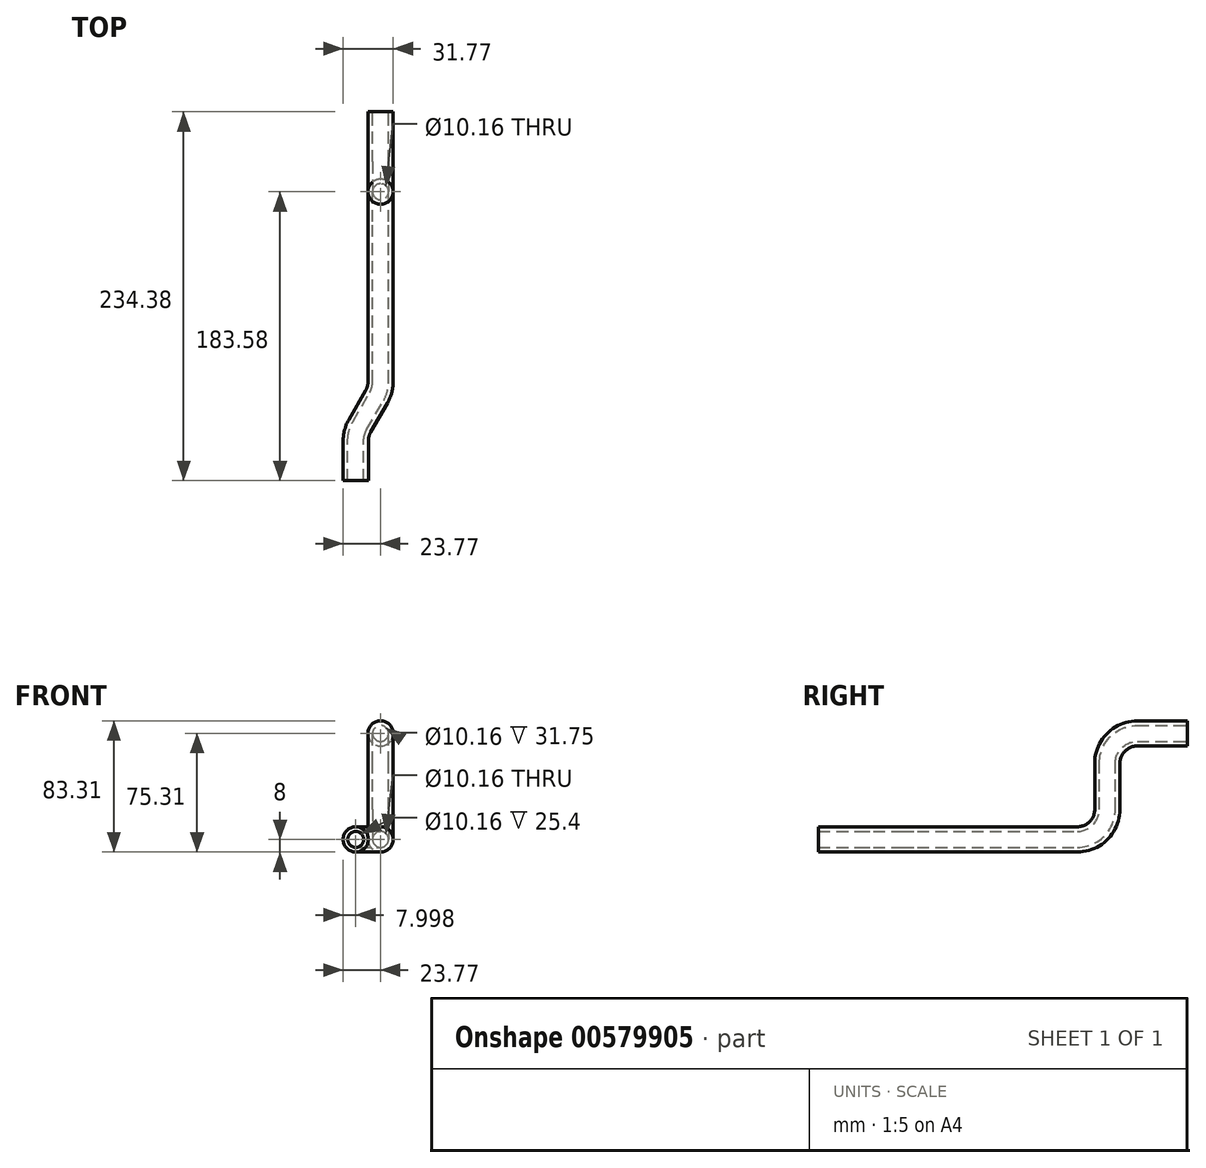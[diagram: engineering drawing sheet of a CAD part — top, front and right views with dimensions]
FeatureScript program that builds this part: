
annotation { "Feature Type Name" : "Feature", "Feature Type Description" : "" }
export const myFeature = defineFeature(function(context is Context, id is Id, definition is map)
    precondition{}
    {
        {
            var Q0;
            Q0=qCreatedBy(makeId("Front.planeOp"),FACE);
            var sketch = newSketch(context, id + "F0", { "sketchPlane" : qUnion([Q0])});
            skCircle(sketch, "E0", {"center": v(0, 0) * mm, "radius": 8 * mm});
            skCircle(sketch, "E1", {"center": v(0, 0) * mm, "radius": 5.08 * mm});
            skSolve(sketch);
        }
        {
            var Q0;
            Q0=qSketchRegion(id+"F0",true);
            extrude(context, id + "F1", {"entities" : qUnion([Q0]), "depth" : 31.75 * mm, "offsetDistance" : 25.4 * mm});
        }
        {
            var Q0;
            Q0=makeQuery(id+"F1.opExtrude","CAP_FACE",FACE,{"disambiguationData":[OSD([sQuery(id+"F0.wireOp",EDGE,"E0"),sQuery(id+"F0.wireOp",EDGE,"E1")])],"isStart":false});
            var sketch = newSketch(context, id + "F2", { "sketchPlane" : qUnion([Q0])});
            skCircle(sketch, "E2", {"center": v(0, 0) * mm, "radius": 8 * mm});
            skCircle(sketch, "E3", {"center": v(0, 0) * mm, "radius": 5.08 * mm});
            skLineSegment(sketch, "E4", {"start": v(-14.6, -19.05) * mm, "end": v(12.81, -19.05) * mm});
            skSolve(sketch);
        }
        {
            var Q0;
            Q0 = qSketchRegion(id + "F2", true);
            var Q1;
            Q1=sQuery(id+"F2.wireOp",EDGE,"E4");
            revolve(context, id + "F3", {"operationType" : NewBodyOperationType.ADD, "entities" : qUnion([Q0]), "axis" : qUnion([Q1]), "revolveType" : RevolveType.ONE_DIRECTION, "angle" : 90 * degree});
        }
        {
            var Q0;
            Q0=makeQuery(id+"F3.opRevolve","CAP_FACE",FACE,{"disambiguationData":[OSD([sQuery(id+"F2.wireOp",EDGE,"E2"),sQuery(id+"F2.wireOp",EDGE,"E3")])],"isStart":false});
            var sketch = newSketch(context, id + "F4", { "sketchPlane" : qUnion([Q0])});
            skCircle(sketch, "E5", {"center": v(0, 50.8) * mm, "radius": 5.08 * mm});
            skCircle(sketch, "E6", {"center": v(0, 50.8) * mm, "radius": 8 * mm});
            skSolve(sketch);
        }
        {
            var Q0;
            Q0 = qSketchRegion(id + "F4", true);
            extrude(context, id + "F5", {"entities" : qUnion([Q0]), "operationType" : NewBodyOperationType.ADD, "depth" : 29.2 * mm, "offsetDistance" : 25.4 * mm});
        }
        {
            var Q0;
            Q0=makeQuery(id+"F5.opExtrude","CAP_FACE",FACE,{"disambiguationData":[OSD([sQuery(id+"F4.wireOp",EDGE,"E5"),sQuery(id+"F4.wireOp",EDGE,"E6")])],"isStart":false});
            var sketch = newSketch(context, id + "F6", { "sketchPlane" : qUnion([Q0])});
            skCircle(sketch, "E7", {"center": v(0, 50.8) * mm, "radius": 5.08 * mm});
            skCircle(sketch, "E8", {"center": v(0, 50.8) * mm, "radius": 8 * mm});
            skLineSegment(sketch, "E9", {"start": v(-25.42, 69.85) * mm, "end": v(16.47, 69.85) * mm});
            skSolve(sketch);
        }
        {
            var Q0;
            Q0 = qSketchRegion(id + "F6", true);
            var Q1;
            Q1=sQuery(id+"F6.wireOp",EDGE,"E9");
            revolve(context, id + "F7", {"operationType" : NewBodyOperationType.ADD, "entities" : qUnion([Q0]), "axis" : qUnion([Q1]), "revolveType" : RevolveType.ONE_DIRECTION, "oppositeDirection" : true, "angle" : 90 * degree});
        }
        {
            var Q0;
            Q0=makeQuery(id+"F7.opRevolve","CAP_FACE",FACE,{"disambiguationData":[OSD([sQuery(id+"F6.wireOp",EDGE,"E7"),sQuery(id+"F6.wireOp",EDGE,"E8")])],"isStart":false});
            var sketch = newSketch(context, id + "F8", { "sketchPlane" : qUnion([Q0])});
            skCircle(sketch, "E10", {"center": v(0, -67.3) * mm, "radius": 5.08 * mm});
            skCircle(sketch, "E11", {"center": v(0, -67.3) * mm, "radius": 8 * mm});
            skSolve(sketch);
        }
        {
            var Q0;
            Q0 = qSketchRegion(id + "F8", true);
            extrude(context, id + "F9", {"entities" : qUnion([Q0]), "operationType" : NewBodyOperationType.ADD, "depth" : 101.6 * mm, "offsetDistance" : 25.4 * mm});
        }
        {
            var Q0;
            Q0=makeQuery(id+"F9.opExtrude","CAP_FACE",FACE,{"disambiguationData":[OSD([sQuery(id+"F8.wireOp",EDGE,"E10"),sQuery(id+"F8.wireOp",EDGE,"E11")])],"isStart":false});
            var sketch = newSketch(context, id + "F10", { "sketchPlane" : qUnion([Q0])});
            skCircle(sketch, "E12", {"center": v(0, -67.3) * mm, "radius": 5.08 * mm});
            skCircle(sketch, "E13", {"center": v(0, -67.3) * mm, "radius": 8 * mm});
            skLineSegment(sketch, "E14", {"start": v(-19.05, -56.51) * mm, "end": v(-19.05, -74.32) * mm});
            skSolve(sketch);
        }
        {
            var Q0;
            Q0 = qSketchRegion(id + "F10", true);
            var Q1;
            Q1=sQuery(id+"F10.wireOp",EDGE,"E14");
            revolve(context, id + "F11", {"operationType" : NewBodyOperationType.ADD, "entities" : qUnion([Q0]), "axis" : qUnion([Q1]), "revolveType" : RevolveType.ONE_DIRECTION, "angle" : 30 * degree});
        }
        {
            var Q0;
            Q0=makeQuery(id+"F11.opRevolve","CAP_FACE",FACE,{"disambiguationData":[OSD([sQuery(id+"F10.wireOp",EDGE,"E12"),sQuery(id+"F10.wireOp",EDGE,"E13")])],"isStart":false});
            var sketch = newSketch(context, id + "F12", { "sketchPlane" : qUnion([Q0])});
            skCircle(sketch, "E15", {"center": v(88.28, -67.3) * mm, "radius": 5.08 * mm});
            skCircle(sketch, "E16", {"center": v(88.28, -67.3) * mm, "radius": 8 * mm});
            skSolve(sketch);
        }
        {
            var Q0;
            Q0 = qSketchRegion(id + "F12", true);
            extrude(context, id + "F13", {"entities" : qUnion([Q0]), "operationType" : NewBodyOperationType.ADD, "depth" : 21.34 * mm, "offsetDistance" : 25.4 * mm});
        }
        {
            var Q0;
            Q0=makeQuery(id+"F13.opExtrude","CAP_FACE",FACE,{"disambiguationData":[OSD([sQuery(id+"F12.wireOp",EDGE,"E15"),sQuery(id+"F12.wireOp",EDGE,"E16")])],"isStart":false});
            var sketch = newSketch(context, id + "F14", { "sketchPlane" : qUnion([Q0])});
            skCircle(sketch, "E17", {"center": v(88.28, -67.3) * mm, "radius": 5.08 * mm});
            skCircle(sketch, "E18", {"center": v(88.28, -67.3) * mm, "radius": 8 * mm});
            skLineSegment(sketch, "E19", {"start": v(107.33, -60.55) * mm, "end": v(107.33, -70.95) * mm});
            skSolve(sketch);
        }
        {
            var Q0;
            Q0 = qSketchRegion(id + "F14", true);
            var Q1;
            Q1=sQuery(id+"F14.wireOp",EDGE,"E19");
            revolve(context, id + "F15", {"operationType" : NewBodyOperationType.ADD, "entities" : qUnion([Q0]), "axis" : qUnion([Q1]), "revolveType" : RevolveType.ONE_DIRECTION, "oppositeDirection" : true, "angle" : 30 * degree});
        }
        {
            var Q0;
            Q0=makeQuery(id+"F15.opRevolve","CAP_FACE",FACE,{"disambiguationData":[OSD([sQuery(id+"F14.wireOp",EDGE,"E17"),sQuery(id+"F14.wireOp",EDGE,"E18")])],"isStart":false});
            var sketch = newSketch(context, id + "F16", { "sketchPlane" : qUnion([Q0])});
            skCircle(sketch, "E20", {"center": v(-15.77, -67.3) * mm, "radius": 5.08 * mm});
            skCircle(sketch, "E21", {"center": v(-15.77, -67.3) * mm, "radius": 8 * mm});
            skSolve(sketch);
        }
        {
            var Q0;
            Q0 = qSketchRegion(id + "F16", true);
            extrude(context, id + "F17", {"entities" : qUnion([Q0]), "operationType" : NewBodyOperationType.ADD, "depth" : 25.4 * mm, "offsetDistance" : 25.4 * mm});
        }
    });
